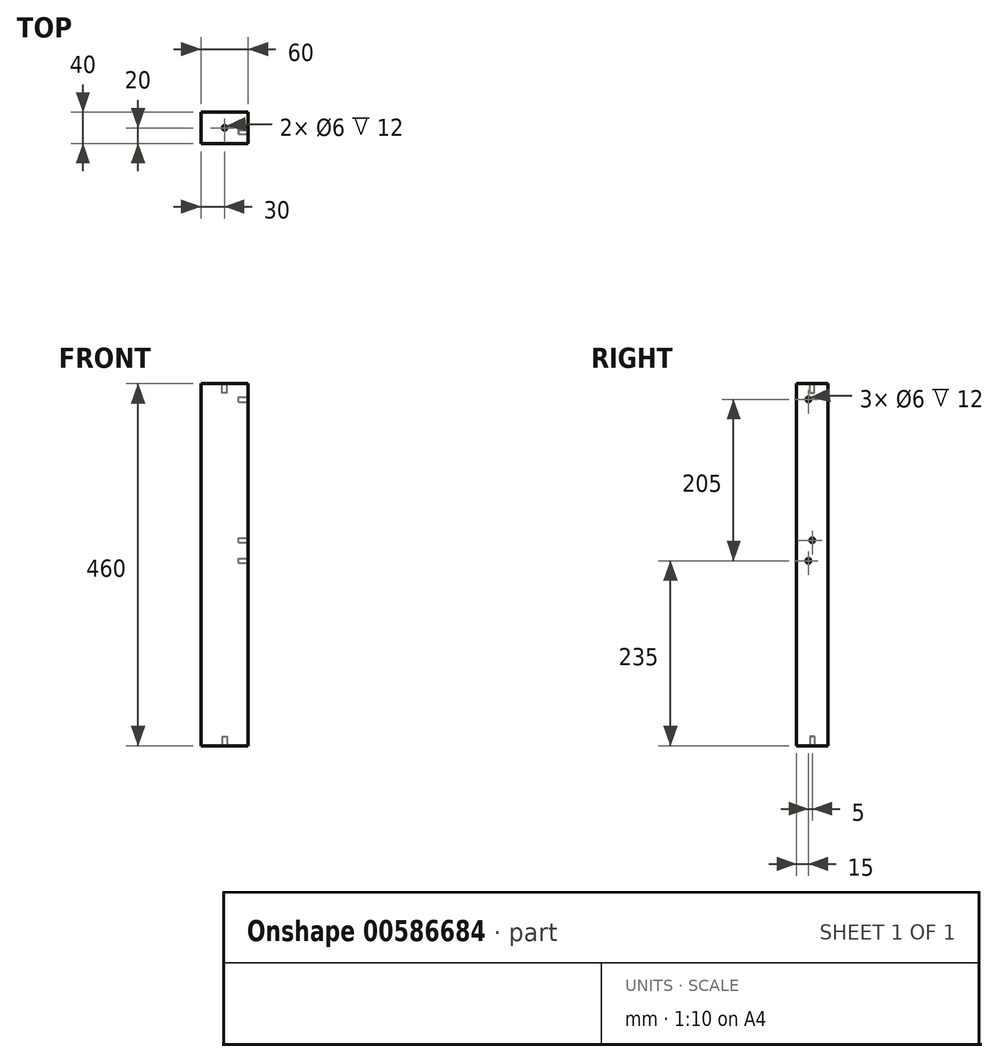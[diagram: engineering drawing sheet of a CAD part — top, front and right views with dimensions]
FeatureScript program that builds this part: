
annotation { "Feature Type Name" : "Feature", "Feature Type Description" : "" }
export const myFeature = defineFeature(function(context is Context, id is Id, definition is map)
    precondition{}
    {
        {
            var Q0;
            Q0=qCreatedBy(makeId("Top.planeOp"),FACE);
            var sketch = newSketch(context, id + "F0", { "sketchPlane" : qUnion([Q0])});
            skLineSegment(sketch, "E0.bottom", {"start": v(0, 0) * mm, "end": v(60, 0) * mm});
            skLineSegment(sketch, "E0.top", {"start": v(0, 40) * mm, "end": v(60, 40) * mm});
            skLineSegment(sketch, "E0.left", {"start": v(0, 0) * mm, "end": v(0, 40) * mm});
            skLineSegment(sketch, "E0.right", {"start": v(60, 0) * mm, "end": v(60, 40) * mm});
            skSolve(sketch);
        }
        {
            var Q0;
            Q0 = qSketchRegion(id + "F0", true);
            extrude(context, id + "F1", {"entities" : qUnion([Q0]), "depth" : 460 * mm, "offsetDistance" : 25 * mm});
        }
        {
            var Q0;
            Q0=makeQuery(id+"F1.opExtrude","CAP_FACE",FACE,{"disambiguationData":[OSD([sQuery(id+"F0.wireOp",EDGE,"E0.bottom"),sQuery(id+"F0.wireOp",EDGE,"E0.top"),sQuery(id+"F0.wireOp",EDGE,"E0.left"),sQuery(id+"F0.wireOp",EDGE,"E0.right")])],"isStart":false});
            var sketch = newSketch(context, id + "F2", { "sketchPlane" : qUnion([Q0])});
            skCircle(sketch, "E1", {"center": v(30, 20) * mm, "radius": 3 * mm});
            skSolve(sketch);
        }
        {
            var Q0;
            Q0 = qSketchRegion(id + "F2", true);
            extrude(context, id + "F3", {"entities" : qUnion([Q0]), "operationType" : NewBodyOperationType.REMOVE, "oppositeDirection" : true, "depth" : 12 * mm, "offsetDistance" : 25 * mm});
        }
        {
            var Q0;
            Q0=makeQuery(id+"F1.opExtrude","CAP_FACE",FACE,{"disambiguationData":[OSD([sQuery(id+"F0.wireOp",EDGE,"E0.bottom"),sQuery(id+"F0.wireOp",EDGE,"E0.top"),sQuery(id+"F0.wireOp",EDGE,"E0.left"),sQuery(id+"F0.wireOp",EDGE,"E0.right")])],"isStart":true});
            var sketch = newSketch(context, id + "F4", { "sketchPlane" : qUnion([Q0])});
            skCircle(sketch, "E2.0", {"center": v(30, -20) * mm, "radius": 3 * mm});
            skSolve(sketch);
        }
        {
            var Q0;
            Q0 = qSketchRegion(id + "F4", true);
            extrude(context, id + "F5", {"entities" : qUnion([Q0]), "operationType" : NewBodyOperationType.REMOVE, "oppositeDirection" : true, "depth" : 12 * mm, "offsetDistance" : 25 * mm});
        }
        {
            var Q0;
            Q0=makeQuery(id+"F1.opExtrude","SWEPT_FACE",FACE,{"disambiguationData":[OSD([sQuery(id+"F0.wireOp",EDGE,"E0.right")])]});
            var sketch = newSketch(context, id + "F6", { "sketchPlane" : qUnion([Q0])});
            skCircle(sketch, "E3", {"center": v(20, 261) * mm, "radius": 3 * mm});
            skSolve(sketch);
        }
        {
            var Q0;
            Q0 = qSketchRegion(id + "F6", true);
            extrude(context, id + "F7", {"entities" : qUnion([Q0]), "operationType" : NewBodyOperationType.REMOVE, "oppositeDirection" : true, "depth" : 12 * mm, "offsetDistance" : 25 * mm});
        }
        {
            var Q0;
            Q0=makeQuery(id+"F1.opExtrude","SWEPT_FACE",FACE,{"disambiguationData":[OSD([sQuery(id+"F0.wireOp",EDGE,"E0.right")])]});
            var sketch = newSketch(context, id + "F8", { "sketchPlane" : qUnion([Q0])});
            skCircle(sketch, "E4", {"center": v(15, 440) * mm, "radius": 3 * mm});
            skSolve(sketch);
        }
        {
            var Q0;
            Q0 = qSketchRegion(id + "F8", true);
            extrude(context, id + "F9", {"entities" : qUnion([Q0]), "operationType" : NewBodyOperationType.REMOVE, "oppositeDirection" : true, "depth" : 12 * mm, "offsetDistance" : 25 * mm});
        }
        {
            var Q0;
            Q0=makeQuery(id+"F1.opExtrude","SWEPT_FACE",FACE,{"disambiguationData":[OSD([sQuery(id+"F0.wireOp",EDGE,"E0.right")])]});
            var sketch = newSketch(context, id + "F10", { "sketchPlane" : qUnion([Q0])});
            skCircle(sketch, "E5", {"center": v(15, 235) * mm, "radius": 3 * mm});
            skSolve(sketch);
        }
        {
            var Q0;
            Q0 = qSketchRegion(id + "F10", true);
            extrude(context, id + "F11", {"entities" : qUnion([Q0]), "operationType" : NewBodyOperationType.REMOVE, "oppositeDirection" : true, "depth" : 12 * mm, "offsetDistance" : 25 * mm});
        }
    });
